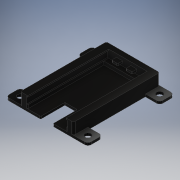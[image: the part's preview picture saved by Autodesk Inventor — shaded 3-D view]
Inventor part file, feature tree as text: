
AUTODESK INVENTOR PART (.ipt)
format: ipt  version: 2019 (Build 230136000, 136)  size: 293,376 bytes
history: native  units: in
note: dims shown in document units (in); Inventor stores cm internally (conversion verified against a paired STEP export)
features: sketch x8, extrude x7, fillet x5
ambient origin geometry x8: Origin, YZ Plane, XZ Plane, XY Plane, X Axis, Y Axis, Z Axis, Center Point
bodies: Solid1 (feature_tree)
feature tree (20):
  extrude  "Base"  Depth=0.35in
  fillet  "Fillet1"  Radius=1.4014in
  sketch  "Sketch2"  dims[d3=0.35in d4=0.35in]
  extrude  "bottom"  Depth=0.35in
  extrude  "Extrusion3"  Depth=0.35in
  extrude  "Extrusion4"  Depth=0.15in
  extrude  "Extrusion5"  Depth=0.175in
  extrude  "Extrusion6"  Depth=0.15in
  extrude  "Extrusion7"  Depth=0.15in
  fillet  "Fillet2"  Radius=0.175in
  fillet  "Fillet3"  Radius=0.175in
  fillet  "Fillet4"  Radius=0.15in
  fillet  "Fillet5"  Radius=0.175in
  sketch  "Sketch1"  dims[d0=0.35in d1=0.35in d2=1.4014in]
  sketch  "Sketch3"  dims[d5=1.65in d6=0.35in]
  sketch  "Sketch4"  dims[d7=0.35in d8=0.15in]
  sketch  "Sketch5"  dims[d9=0.175in d10=0.175in]
  sketch  "Sketch6"  dims[d11=0.15in d12=0.175in]
  sketch  "Sketch7"  dims[d13=0.175in d14=0.15in d15=0.175in d16=0.175in d17=0.15in d18=0.175in]
  sketch  "Sketch8"  dims[d19=0.175in d20=0.0591in d21=0.0in d22=0.0787in d23=0.1801in d24=0.125in d25=0.1801in d26=0.085in d27=0.0in d28=0.15in d29=0.15in d30=0.125in d31=0.1634in d32=0.0in d33=0.0315in d34=0.0315in d35=0.0295in d36=0.0in d37=0.3051in d38=0.3159in d39=0.5906in d40=0.0787in d41=0.0in d42=0.1181in d43=0.0787in d44=0.0in d45=0.065in d46=0.065in d47=0.2in d48=0.15in d49=0.15in d50=0.0492in d51=0.0492in d52=0.22in d53=0.15in d54=0.0in d55=0.0197in d56=0.0197in d57=0.0197in d58=0.0394in]
